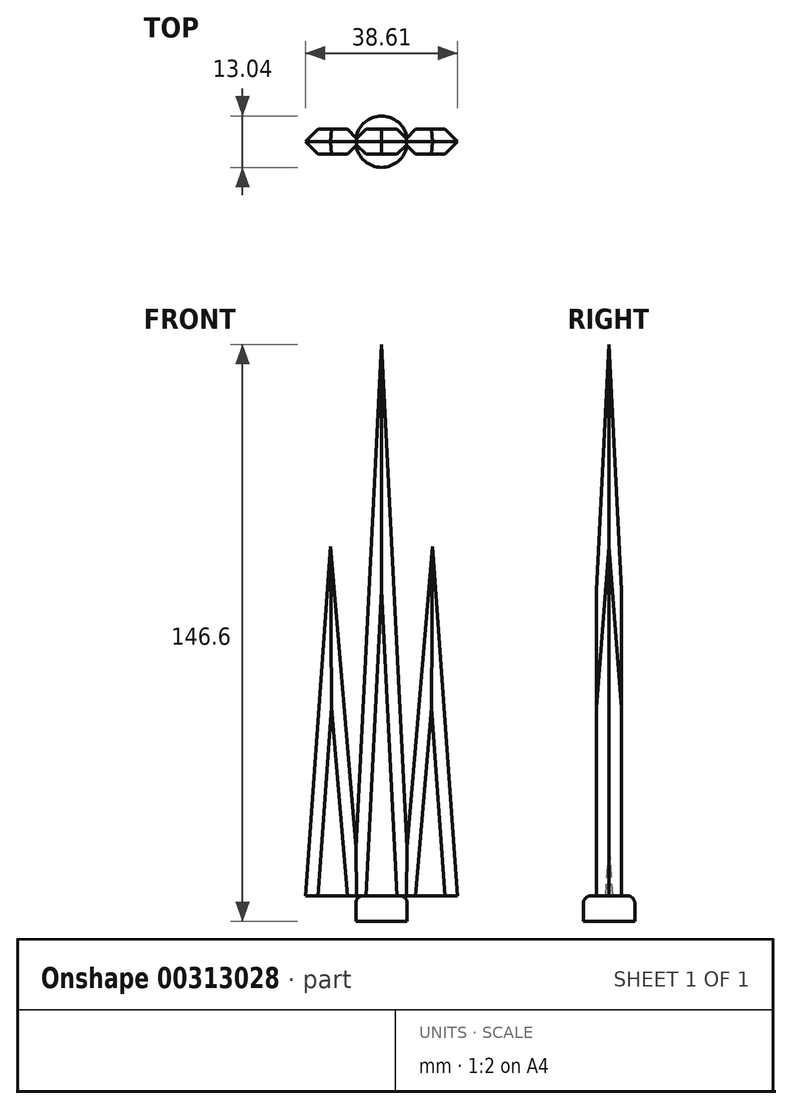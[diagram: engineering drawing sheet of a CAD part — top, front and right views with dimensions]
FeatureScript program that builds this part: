
annotation { "Feature Type Name" : "Feature", "Feature Type Description" : "" }
export const myFeature = defineFeature(function(context is Context, id is Id, definition is map)
    precondition{}
    {
        {
            var Q0;
            Q0=qCreatedBy(makeId("Front.planeOp"),FACE);
            var sketch = newSketch(context, id + "F0", { "sketchPlane" : qUnion([Q0])});
            skLineSegment(sketch, "E0", {"start": v(12.33, 10.53) * mm, "end": v(12.33, 17.04) * mm});
            skLineSegment(sketch, "E1", {"start": v(-0.7, 17.04) * mm, "end": v(-0.7, 10.53) * mm});
            skLineSegment(sketch, "E2", {"start": v(-0.7, 10.53) * mm, "end": v(12.33, 10.53) * mm});
            skLineSegment(sketch, "E3", {"start": v(-0.7, 17.04) * mm, "end": v(12.33, 17.04) * mm});
            skLineSegment(sketch, "E4", {"start": v(-0.7, 17.04) * mm, "end": v(-13.51, 17.04) * mm});
            skLineSegment(sketch, "E5", {"start": v(-13.51, 17.04) * mm, "end": v(-7.1, 105.74) * mm});
            skPoint(sketch, "E5.endSnap0", {"position": v(-7.1, 17.04) * mm});
            skPoint(sketch, "E6.endSnap0", {"position": v(5.82, 17.04) * mm});
            skLineSegment(sketch, "E7", {"start": v(12.33, 17.04) * mm, "end": v(25.1, 17.04) * mm});
            skLineSegment(sketch, "E8", {"start": v(25.1, 17.04) * mm, "end": v(18.72, 105.74) * mm});
            skPoint(sketch, "E8.endSnap0", {"position": v(18.72, 17.04) * mm});
            skLineSegment(sketch, "E9", {"start": v(-7.1, 105.74) * mm, "end": v(-0.7, 29.3) * mm});
            skLineSegment(sketch, "E10", {"start": v(-0.7, 29.3) * mm, "end": v(5.82, 157.13) * mm});
            skLineSegment(sketch, "E11", {"start": v(5.82, 157.13) * mm, "end": v(12.33, 29.3) * mm});
            skLineSegment(sketch, "E12", {"start": v(12.33, 29.3) * mm, "end": v(18.72, 105.74) * mm});
            skLineSegment(sketch, "E13", {"start": v(5.82, 17.04) * mm, "end": v(5.82, 10.53) * mm});
            skSolve(sketch);
        }
        {
            var Q0;
            Q0=makeQuery(id+"F0.imprint","IMPRINT",FACE,{"disambiguationData":[TD([[makeQuery(id+"F0.imprint","IMPRINT",EDGE,{"derivedFrom":sQuery(id+"F0.wireOp",EDGE,"E3")}),1.0]])]});
            extrude(context, id + "F1", {"entities" : qUnion([Q0]), "endBound" : BoundingType.SYMMETRIC, "depth" : 6.35 * mm});
        }
        {
            var Q0;
            {var subQ0=sQuery(id+"F0.wireOp",EDGE,"E1");Q0=makeQuery(id+"F0.imprint","IMPRINT",FACE,{"disambiguationData":[TD([[makeQuery(id+"F0.imprint","IMPRINT",EDGE,{"derivedFrom":subQ0}),1.0]])]});}
            var Q1;
            Q1=sQuery(id+"F0.wireOp",EDGE,"E13");
            revolve(context, id + "F2", {"entities" : qUnion([Q0]), "axis" : qUnion([Q1]), "revolveType" : RevolveType.FULL});
        }
        {
            var Q0;
            Q0=makeQuery(id+"F2.opRevolve","SWEPT_EDGE",EDGE,{"disambiguationData":[OSD([sQuery(id+"F0.wireOp",EDGE,"E1"),sQuery(id+"F0.wireOp",EDGE,"E3"),sQuery(id+"F0.wireOp",EDGE,"E4")])]});
            fillet(context, id + "F3", {"entities" : qUnion([Q0]), "radius" : 1.84 * mm, "tangentPropagation" : true, "allowEdgeOverflow" : false});
        }
        {
            var Q0;
            Q0=makeQuery(id+"F1.opExtrude","CAP_EDGE",EDGE,{"disambiguationData":[OSD([sQuery(id+"F0.wireOp",EDGE,"E5")])],"isStart":false});
            var Q1;
            Q1=makeQuery(id+"F1.opExtrude","CAP_EDGE",EDGE,{"disambiguationData":[OSD([sQuery(id+"F0.wireOp",EDGE,"E5")])],"isStart":true});
            var Q2;
            Q2=makeQuery(id+"F1.opExtrude","CAP_EDGE",EDGE,{"disambiguationData":[OSD([sQuery(id+"F0.wireOp",EDGE,"E10")])],"isStart":false});
            var Q3;
            Q3=makeQuery(id+"F1.opExtrude","CAP_EDGE",EDGE,{"disambiguationData":[OSD([sQuery(id+"F0.wireOp",EDGE,"E11")])],"isStart":false});
            var Q4;
            Q4=makeQuery(id+"F1.opExtrude","CAP_EDGE",EDGE,{"disambiguationData":[OSD([sQuery(id+"F0.wireOp",EDGE,"E12")])],"isStart":false});
            var Q5;
            Q5=makeQuery(id+"F1.opExtrude","CAP_EDGE",EDGE,{"disambiguationData":[OSD([sQuery(id+"F0.wireOp",EDGE,"E8")])],"isStart":false});
            var Q6;
            Q6=makeQuery(id+"F1.opExtrude","CAP_EDGE",EDGE,{"disambiguationData":[OSD([sQuery(id+"F0.wireOp",EDGE,"E9")])],"isStart":false});
            var Q7;
            Q7=makeQuery(id+"F1.opExtrude","CAP_EDGE",EDGE,{"disambiguationData":[OSD([sQuery(id+"F0.wireOp",EDGE,"E8")])],"isStart":true});
            var Q8;
            Q8=makeQuery(id+"F1.opExtrude","CAP_EDGE",EDGE,{"disambiguationData":[OSD([sQuery(id+"F0.wireOp",EDGE,"E12")])],"isStart":true});
            var Q9;
            Q9=makeQuery(id+"F1.opExtrude","CAP_EDGE",EDGE,{"disambiguationData":[OSD([sQuery(id+"F0.wireOp",EDGE,"E11")])],"isStart":true});
            var Q10;
            Q10=makeQuery(id+"F1.opExtrude","CAP_EDGE",EDGE,{"disambiguationData":[OSD([sQuery(id+"F0.wireOp",EDGE,"E10")])],"isStart":true});
            var Q11;
            Q11=makeQuery(id+"F1.opExtrude","CAP_EDGE",EDGE,{"disambiguationData":[OSD([sQuery(id+"F0.wireOp",EDGE,"E9")])],"isStart":true});
            chamfer(context, id + "F4", {"entities" : qUnion([Q0, Q1, Q2, Q3, Q4, Q5, Q6, Q7, Q8, Q9, Q10, Q11]), "width" : 3.17 * mm, "tangentPropagation" : true});
        }
    });
